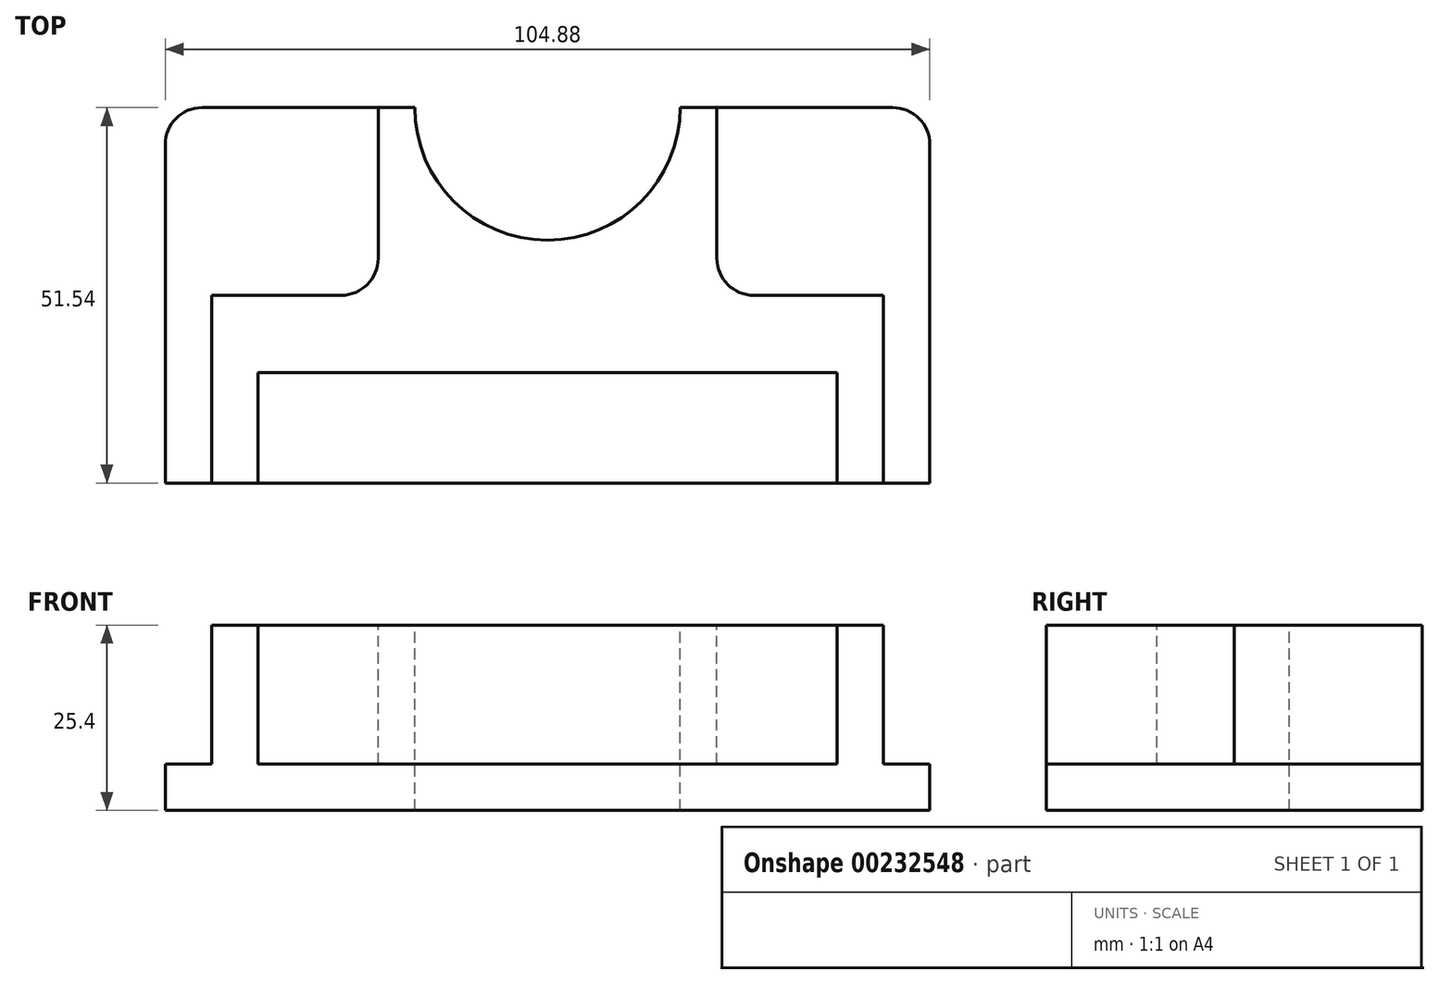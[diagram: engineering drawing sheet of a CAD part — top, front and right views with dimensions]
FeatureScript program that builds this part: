
annotation { "Feature Type Name" : "Feature", "Feature Type Description" : "" }
export const myFeature = defineFeature(function(context is Context, id is Id, definition is map)
    precondition{}
    {
        {
            var Q0;
            Q0=qCreatedBy(makeId("Top.planeOp"),FACE);
            var sketch = newSketch(context, id + "F0", { "sketchPlane" : qUnion([Q0])});
            skLineSegment(sketch, "E0.bottom", {"start": v(52.44, 25.77) * mm, "end": v(-52.44, 25.77) * mm});
            skLineSegment(sketch, "E0.top", {"start": v(52.44, -25.77) * mm, "end": v(-52.44, -25.77) * mm});
            skLineSegment(sketch, "E0.left", {"start": v(52.44, 25.77) * mm, "end": v(52.44, -25.77) * mm});
            skLineSegment(sketch, "E0.right", {"start": v(-52.44, 25.77) * mm, "end": v(-52.44, -25.77) * mm});
            skPoint(sketch, "E0.middle", {"position": v(0, 0) * mm});
            skSolve(sketch);
        }
        {
            var Q0;
            Q0=makeQuery(id+"F0.imprint","IMPRINT",FACE,{"disambiguationData":[TD([[makeQuery(id+"F0.imprint","IMPRINT",EDGE,{"derivedFrom":sQuery(id+"F0.wireOp",EDGE,"E0.bottom")}),1.0]])]});
            extrude(context, id + "F1", {"entities" : qUnion([Q0]), "depth" : 25.4 * mm});
        }
        {
            var Q0;
            Q0=makeQuery(id+"F1.opExtrude","SWEPT_EDGE",EDGE,{"disambiguationData":[OSD([sQuery(id+"F0.wireOp",EDGE,"E0.bottom"),sQuery(id+"F0.wireOp",EDGE,"E0.right")])]});
            var Q1;
            Q1=makeQuery(id+"F1.opExtrude","SWEPT_EDGE",EDGE,{"disambiguationData":[OSD([sQuery(id+"F0.wireOp",EDGE,"E0.bottom"),sQuery(id+"F0.wireOp",EDGE,"E0.left")])]});
            fillet(context, id + "F2", {"entities" : qUnion([Q0, Q1]), "radius" : 5.08 * mm, "tangentPropagation" : true, "allowEdgeOverflow" : false});
        }
        {
            var Q0;
            Q0=makeQuery(id+"F1.opExtrude","CAP_FACE",FACE,{"disambiguationData":[OSD([sQuery(id+"F0.wireOp",EDGE,"E0.bottom"),sQuery(id+"F0.wireOp",EDGE,"E0.top"),sQuery(id+"F0.wireOp",EDGE,"E0.left"),sQuery(id+"F0.wireOp",EDGE,"E0.right")])],"isStart":false});
            var sketch = newSketch(context, id + "F3", { "sketchPlane" : qUnion([Q0])});
            skLineSegment(sketch, "E1.bottom", {"start": v(-39.74, -25.77) * mm, "end": v(39.74, -25.77) * mm});
            skLineSegment(sketch, "E1.top", {"start": v(-39.74, -10.62) * mm, "end": v(39.74, -10.62) * mm});
            skLineSegment(sketch, "E1.left", {"start": v(-39.74, -25.77) * mm, "end": v(-39.74, -10.62) * mm});
            skLineSegment(sketch, "E1.right", {"start": v(39.74, -25.77) * mm, "end": v(39.74, -10.62) * mm});
            skSolve(sketch);
        }
        {
            var Q0;
            Q0 = qSketchRegion(id + "F3", true);
            extrude(context, id + "F4", {"entities" : qUnion([Q0]), "operationType" : NewBodyOperationType.REMOVE, "oppositeDirection" : true, "depth" : 19.05 * mm});
        }
        {
            var Q0;
            Q0=makeQuery(id+"F1.opExtrude","CAP_FACE",FACE,{"disambiguationData":[OSD([sQuery(id+"F0.wireOp",EDGE,"E0.bottom"),sQuery(id+"F0.wireOp",EDGE,"E0.top"),sQuery(id+"F0.wireOp",EDGE,"E0.left"),sQuery(id+"F0.wireOp",EDGE,"E0.right")])],"isStart":false});
            var sketch = newSketch(context, id + "F5", { "sketchPlane" : qUnion([Q0])});
            skCircle(sketch, "E2", {"center": v(0, 25.77) * mm, "radius": 18.2 * mm});
            skSolve(sketch);
        }
        {
            var Q0;
            {var subQ0=sQuery(id+"F5.wireOp",EDGE,"E2");var subQ1=makeQuery(id+"F1.opExtrude","CAP_EDGE",EDGE,{"disambiguationData":[OSD([sQuery(id+"F0.wireOp",EDGE,"E0.bottom")])],"isStart":false});var subQ2=makeQuery(id+"F5.imprint","INTERSECT",VERTEX,{"disambiguationData":[OD(0.0)],"derivedFrom":[subQ1,subQ0]});Q0=makeQuery(id+"F5.imprint","IMPRINT",FACE,{"disambiguationData":[TD([[makeQuery(id+"F5.imprint","IMPRINT",EDGE,{"disambiguationData":[TD([[subQ2,1.0]])],"derivedFrom":subQ0}),1.0]])]});}
            extrude(context, id + "F6", {"entities" : qUnion([Q0]), "operationType" : NewBodyOperationType.REMOVE, "oppositeDirection" : true, "depth" : 25.4 * mm});
        }
        {
            var Q0;
            Q0=makeQuery(id+"F1.opExtrude","CAP_FACE",FACE,{"disambiguationData":[OSD([sQuery(id+"F0.wireOp",EDGE,"E0.bottom"),sQuery(id+"F0.wireOp",EDGE,"E0.top"),sQuery(id+"F0.wireOp",EDGE,"E0.left"),sQuery(id+"F0.wireOp",EDGE,"E0.right")])],"isStart":false});
            var sketch = newSketch(context, id + "F7", { "sketchPlane" : qUnion([Q0])});
            skLineSegment(sketch, "E3.bottom", {"start": v(-52.44, -25.77) * mm, "end": v(-46.1, -25.77) * mm});
            skLineSegment(sketch, "E3.top", {"start": v(-52.44, 25.77) * mm, "end": v(-46.1, 25.77) * mm});
            skLineSegment(sketch, "E3.left", {"start": v(-52.44, -25.77) * mm, "end": v(-52.44, 25.77) * mm});
            skLineSegment(sketch, "E3.right", {"start": v(-46.1, -25.77) * mm, "end": v(-46.1, 25.77) * mm});
            skLineSegment(sketch, "E4.bottom", {"start": v(52.44, -25.77) * mm, "end": v(46.1, -25.77) * mm});
            skLineSegment(sketch, "E4.top", {"start": v(52.44, 25.77) * mm, "end": v(46.1, 25.77) * mm});
            skLineSegment(sketch, "E4.left", {"start": v(52.44, -25.77) * mm, "end": v(52.44, 25.77) * mm});
            skLineSegment(sketch, "E4.right", {"start": v(46.1, -25.77) * mm, "end": v(46.1, 25.77) * mm});
            skSolve(sketch);
        }
        {
            var Q0;
            Q0 = qSketchRegion(id + "F7", true);
            extrude(context, id + "F8", {"entities" : qUnion([Q0]), "operationType" : NewBodyOperationType.REMOVE, "oppositeDirection" : true, "depth" : 19.05 * mm});
        }
        {
            var Q0;
            Q0=makeQuery(id+"F1.opExtrude","CAP_FACE",FACE,{"disambiguationData":[OSD([sQuery(id+"F0.wireOp",EDGE,"E0.bottom"),sQuery(id+"F0.wireOp",EDGE,"E0.top"),sQuery(id+"F0.wireOp",EDGE,"E0.left"),sQuery(id+"F0.wireOp",EDGE,"E0.right")])],"isStart":false});
            var sketch = newSketch(context, id + "F9", { "sketchPlane" : qUnion([Q0])});
            skPoint(sketch, "E5.oppositeSnap0", {"position": v(-46.1, 0) * mm});
            skLineSegment(sketch, "E5.bottom", {"start": v(-46.1, 25.77) * mm, "end": v(-23.23, 25.77) * mm});
            skLineSegment(sketch, "E5.top", {"start": v(-46.1, 0) * mm, "end": v(-23.23, 0) * mm});
            skLineSegment(sketch, "E5.left", {"start": v(-46.1, 25.77) * mm, "end": v(-46.1, 0) * mm});
            skLineSegment(sketch, "E5.right", {"start": v(-23.23, 25.77) * mm, "end": v(-23.23, 0) * mm});
            skLineSegment(sketch, "E6.bottom", {"start": v(46.1, 25.77) * mm, "end": v(23.23, 25.77) * mm});
            skLineSegment(sketch, "E6.top", {"start": v(46.1, 0) * mm, "end": v(23.23, 0) * mm});
            skLineSegment(sketch, "E6.left", {"start": v(46.1, 25.77) * mm, "end": v(46.1, 0) * mm});
            skLineSegment(sketch, "E6.right", {"start": v(23.23, 25.77) * mm, "end": v(23.23, 0) * mm});
            skSolve(sketch);
        }
        {
            var Q0;
            Q0=makeQuery(id+"F9.imprint","IMPRINT",FACE,{"disambiguationData":[TD([[makeQuery(id+"F9.imprint","IMPRINT",EDGE,{"derivedFrom":sQuery(id+"F9.wireOp",EDGE,"E5.bottom")}),1.0]])]});
            var Q1;
            Q1=makeQuery(id+"F9.imprint","IMPRINT",FACE,{"disambiguationData":[TD([[makeQuery(id+"F9.imprint","IMPRINT",EDGE,{"derivedFrom":sQuery(id+"F9.wireOp",EDGE,"E6.bottom")}),1.0]])]});
            extrude(context, id + "F10", {"entities" : qUnion([Q0, Q1]), "operationType" : NewBodyOperationType.REMOVE, "oppositeDirection" : true, "depth" : 19.05 * mm});
        }
        {
            var Q0;
            Q0=makeQuery(id+"F10.boolean.opBoolean","COPY",EDGE,{"derivedFrom":makeQuery(id+"F10.opExtrude","SWEPT_EDGE",EDGE,{"disambiguationData":[OSD([sQuery(id+"F9.wireOp",EDGE,"E5.top"),sQuery(id+"F9.wireOp",EDGE,"E5.right")])]})});
            var Q1;
            Q1=makeQuery(id+"F10.boolean.opBoolean","COPY",EDGE,{"derivedFrom":makeQuery(id+"F10.opExtrude","SWEPT_EDGE",EDGE,{"disambiguationData":[OSD([sQuery(id+"F9.wireOp",EDGE,"E6.top"),sQuery(id+"F9.wireOp",EDGE,"E6.right")])]})});
            fillet(context, id + "F11", {"entities" : qUnion([Q0, Q1]), "radius" : 5.08 * mm, "tangentPropagation" : true, "allowEdgeOverflow" : false});
        }
    });
